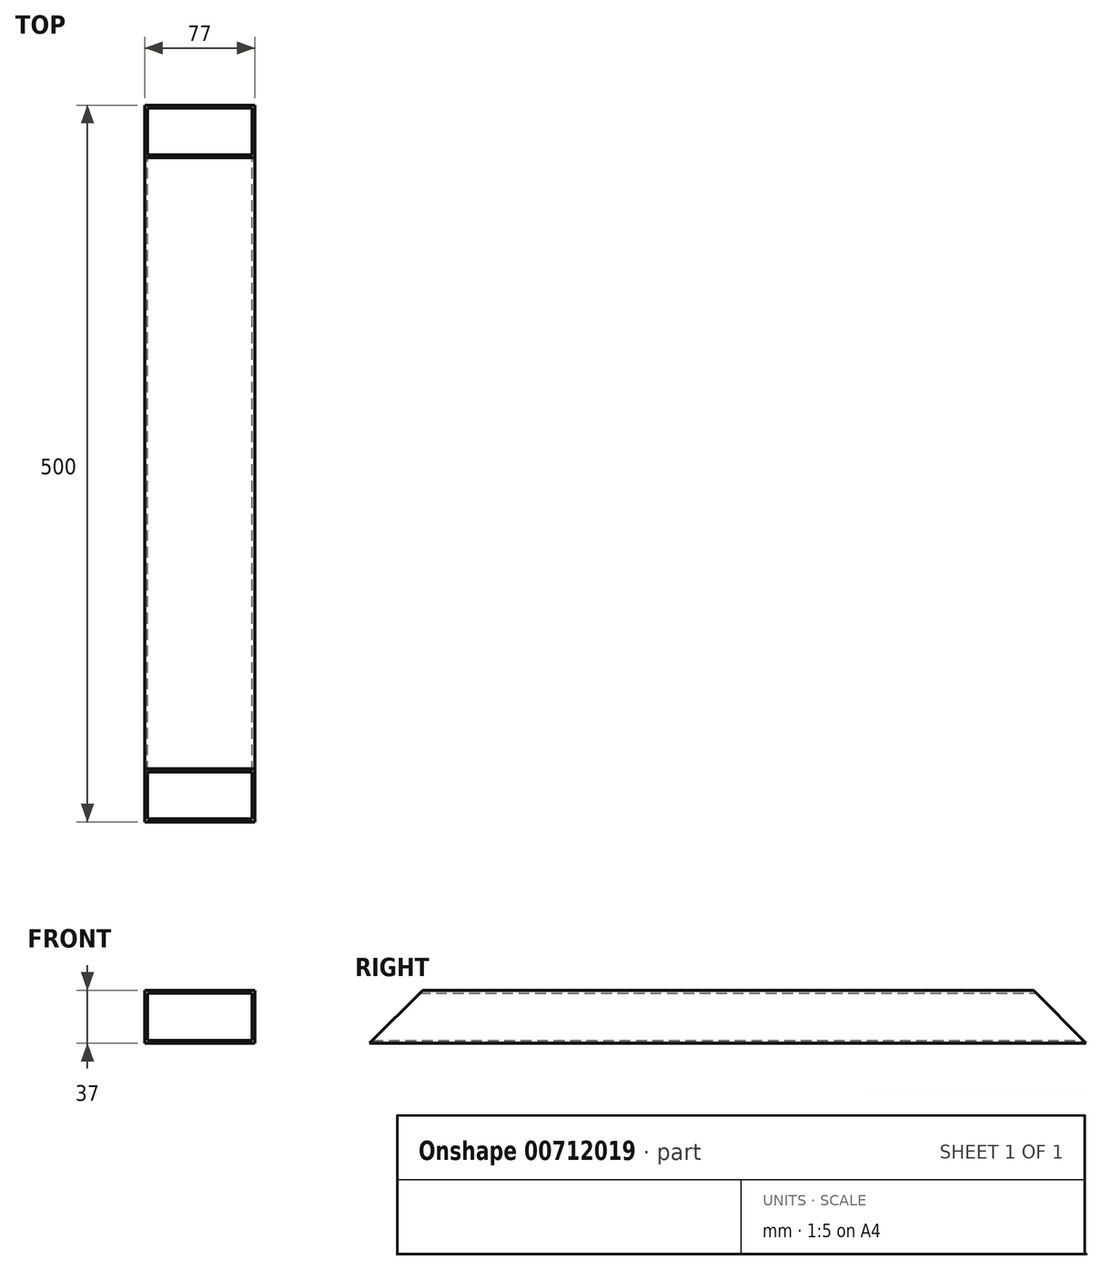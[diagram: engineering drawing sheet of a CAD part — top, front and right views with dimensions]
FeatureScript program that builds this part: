
annotation { "Feature Type Name" : "Feature", "Feature Type Description" : "" }
export const myFeature = defineFeature(function(context is Context, id is Id, definition is map)
    precondition{}
    {
        {
            var Q0;
            Q0=qCreatedBy(makeId("Front.planeOp"),FACE);
            var sketch = newSketch(context, id + "F0", { "sketchPlane" : qUnion([Q0])});
            skLineSegment(sketch, "E0.bottom", {"start": v(0, 0) * mm, "end": v(77, 0) * mm});
            skLineSegment(sketch, "E0.top", {"start": v(0, -37) * mm, "end": v(77, -37) * mm});
            skLineSegment(sketch, "E0.left", {"start": v(0, 0) * mm, "end": v(0, -37) * mm});
            skLineSegment(sketch, "E0.right", {"start": v(77, 0) * mm, "end": v(77, -37) * mm});
            skLineSegment(sketch, "E1.0", {"start": v(2, -2) * mm, "end": v(75, -2) * mm});
            skLineSegment(sketch, "E1.1", {"start": v(2, -2) * mm, "end": v(2, -35) * mm});
            skLineSegment(sketch, "E1.2", {"start": v(2, -35) * mm, "end": v(75, -35) * mm});
            skLineSegment(sketch, "E1.3", {"start": v(75, -2) * mm, "end": v(75, -35) * mm});
            skSolve(sketch);
        }
        {
            var Q0;
            Q0=qSketchRegion(id+"F0",true);
            extrude(context, id + "F1", {"entities" : qUnion([Q0]), "depth" : 500 * mm, "offsetDistance" : 25 * mm});
        }
        {
            var Q0;
            Q0=makeQuery(id+"F1.opExtrude","SWEPT_FACE",FACE,{"disambiguationData":[OSD([sQuery(id+"F0.wireOp",EDGE,"E0.left")])]});
            var sketch = newSketch(context, id + "F2", { "sketchPlane" : qUnion([Q0])});
            skLineSegment(sketch, "E2", {"start": v(0, 0) * mm, "end": v(37, 0) * mm});
            skLineSegment(sketch, "E3", {"start": v(0, 0) * mm, "end": v(0, -37) * mm});
            skLineSegment(sketch, "E4", {"start": v(0, -37) * mm, "end": v(0, -37) * mm});
            skLineSegment(sketch, "E5", {"start": v(36.7, 0.17) * mm, "end": v(0, -37) * mm});
            skSolve(sketch);
        }
        {
            var Q0;
            Q0 = qSketchRegion(id + "F2", true);
            extrude(context, id + "F3", {"entities" : qUnion([Q0]), "operationType" : NewBodyOperationType.REMOVE, "oppositeDirection" : true, "depth" : 128.28 * mm, "offsetDistance" : 25 * mm});
        }
        {
            var Q0;
            Q0=makeQuery(id+"F1.opExtrude","SWEPT_FACE",FACE,{"disambiguationData":[OSD([sQuery(id+"F0.wireOp",EDGE,"E0.right")])]});
            var sketch = newSketch(context, id + "F4", { "sketchPlane" : qUnion([Q0])});
            skLineSegment(sketch, "E6", {"start": v(-500, 0) * mm, "end": v(-500, -37) * mm});
            skLineSegment(sketch, "E7", {"start": v(-500, -37) * mm, "end": v(-500, 0) * mm});
            skLineSegment(sketch, "E8", {"start": v(-463, 0) * mm, "end": v(-500, 0) * mm});
            skLineSegment(sketch, "E9", {"start": v(-500, -37) * mm, "end": v(-463, 0) * mm});
            skSolve(sketch);
        }
        {
            var Q0;
            Q0 = qSketchRegion(id + "F4", true);
            extrude(context, id + "F5", {"entities" : qUnion([Q0]), "operationType" : NewBodyOperationType.REMOVE, "oppositeDirection" : true, "depth" : 87.85 * mm, "offsetDistance" : 25 * mm});
        }
    });
